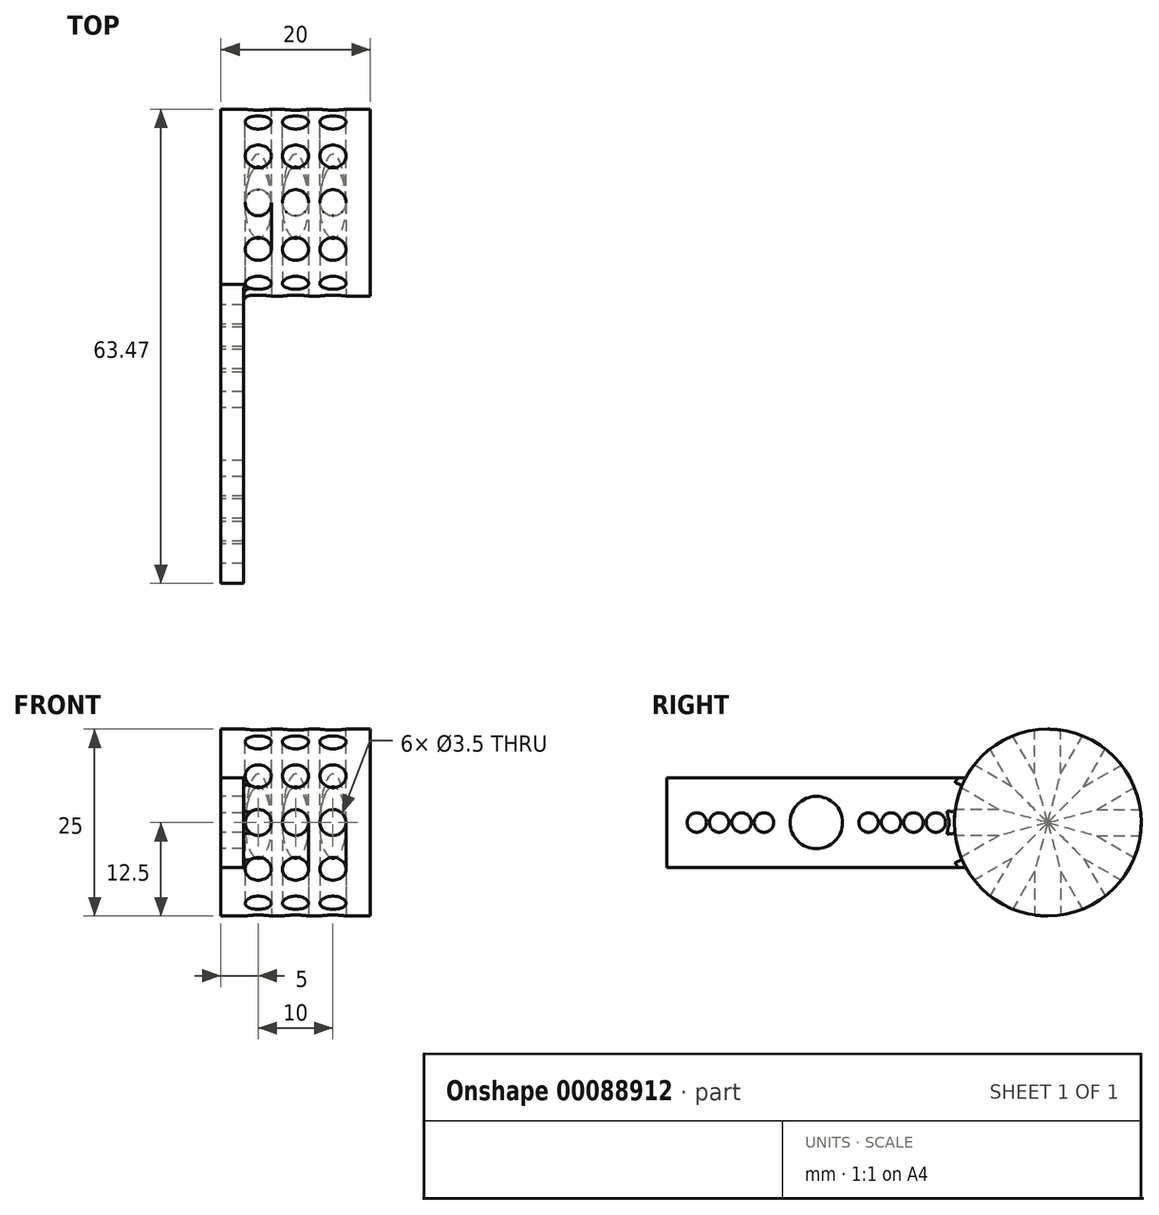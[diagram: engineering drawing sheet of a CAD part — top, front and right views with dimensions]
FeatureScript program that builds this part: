
annotation { "Feature Type Name" : "Feature", "Feature Type Description" : "" }
export const myFeature = defineFeature(function(context is Context, id is Id, definition is map)
    precondition{}
    {
        {
            var Q0;
            Q0=qCreatedBy(makeId("Right.planeOp"),FACE);
            var sketch = newSketch(context, id + "F0", { "sketchPlane" : qUnion([Q0])});
            skLineSegment(sketch, "E0.bottom", {"start": v(0, 12) * mm, "end": v(40, 12) * mm});
            skLineSegment(sketch, "E0.top", {"start": v(0, 0) * mm, "end": v(40, 0) * mm});
            skLineSegment(sketch, "E0.left", {"start": v(0, 12) * mm, "end": v(0, 0) * mm});
            skLineSegment(sketch, "E0.right", {"start": v(40, 12) * mm, "end": v(40, 0) * mm});
            skLineSegment(sketch, "E1", {"start": v(-4.67, 6) * mm, "end": v(58.67, 6) * mm, "construction": true});
            skLineSegment(sketch, "E2", {"start": v(20, 18.3) * mm, "end": v(20, -9.77) * mm, "construction": true});
            skCircle(sketch, "E3", {"center": v(20, 6) * mm, "radius": 3.5 * mm});
            skCircle(sketch, "E4", {"center": v(27, 6) * mm, "radius": 1.3 * mm});
            skCircle(sketch, "E5.1.0.0", {"center": v(30, 6) * mm, "radius": 1.3 * mm});
            skCircle(sketch, "E5.2.0.0", {"center": v(33, 6) * mm, "radius": 1.3 * mm});
            skCircle(sketch, "E5.3.0.0", {"center": v(36, 6) * mm, "radius": 1.3 * mm});
            skLineSegment(sketch, "E5.direction1", {"start": v(27, 6) * mm, "end": v(30, 6) * mm, "construction": true});
            skCircle(sketch, "E6.MirrorC", {"center": v(4, 6) * mm, "radius": 1.3 * mm});
            skCircle(sketch, "E7.MirrorC", {"center": v(7, 6) * mm, "radius": 1.3 * mm});
            skCircle(sketch, "E8.MirrorC", {"center": v(10, 6) * mm, "radius": 1.3 * mm});
            skCircle(sketch, "E9.MirrorC", {"center": v(13, 6) * mm, "radius": 1.3 * mm});
            skSolve(sketch);
        }
        {
            var Q0;
            Q0 = qSketchRegion(id + "F0", true);
            extrude(context, id + "F1", {"entities" : qUnion([Q0]), "depth" : 3 * mm});
        }
        {
            var Q0;
            Q0=makeQuery(id+"F1.opExtrude","CAP_FACE",FACE,{"disambiguationData":[OSD([sQuery(id+"F0.wireOp",EDGE,"E0.bottom"),sQuery(id+"F0.wireOp",EDGE,"E0.top"),sQuery(id+"F0.wireOp",EDGE,"E0.left"),sQuery(id+"F0.wireOp",EDGE,"E0.right"),sQuery(id+"F0.wireOp",EDGE,"E3"),sQuery(id+"F0.wireOp",EDGE,"E4"),sQuery(id+"F0.wireOp",EDGE,"E5.1.0.0"),sQuery(id+"F0.wireOp",EDGE,"E5.2.0.0"),sQuery(id+"F0.wireOp",EDGE,"E5.3.0.0"),sQuery(id+"F0.wireOp",EDGE,"E6.MirrorC"),sQuery(id+"F0.wireOp",EDGE,"E7.MirrorC"),sQuery(id+"F0.wireOp",EDGE,"E8.MirrorC"),sQuery(id+"F0.wireOp",EDGE,"E9.MirrorC")])],"isStart":true});
            var sketch = newSketch(context, id + "F2", { "sketchPlane" : qUnion([Q0])});
            skCircle(sketch, "E10", {"center": v(-50.97, 6) * mm, "radius": 12.5 * mm});
            skSolve(sketch);
        }
        {
            var Q0;
            Q0 = qSketchRegion(id + "F2", true);
            extrude(context, id + "F3", {"entities" : qUnion([Q0]), "operationType" : NewBodyOperationType.ADD, "oppositeDirection" : true, "depth" : 20 * mm});
        }
        {
            var Q0;
            Q0=makeQuery(id+"F1.opExtrude","SWEPT_FACE",FACE,{"disambiguationData":[OSD([sQuery(id+"F0.wireOp",EDGE,"E0.bottom")])]});
            var Q1;
            Q1=makeQuery(id+"F1.opExtrude","SWEPT_FACE",FACE,{"disambiguationData":[OSD([sQuery(id+"F0.wireOp",EDGE,"E0.top")])]});
            cPlane(context, id + "F4", {"entities" : qUnion([Q0, Q1]), "cplaneType" : CPlaneType.MID_PLANE, "offset" : 150 * mm, "width" : 150 * mm, "height" : 150 * mm});
        }
        {
            var Q0;
            Q0=qCreatedBy(id+"F4.planeOp",FACE);
            cPlane(context, id + "F5", {"entities" : qUnion([Q0]), "cplaneType" : CPlaneType.OFFSET, "offset" : 12.5 * mm, "width" : 150 * mm, "height" : 150 * mm});
        }
        {
            var Q0;
            Q0=qCreatedBy(id+"F5.planeOp",FACE);
            var sketch = newSketch(context, id + "F6", { "sketchPlane" : qUnion([Q0])});
            skLineSegment(sketch, "E11", {"start": v(-38.02, 50.97) * mm, "end": v(35.5, 50.97) * mm, "construction": true});
            skCircle(sketch, "E12", {"center": v(10, 50.97) * mm, "radius": 1.75 * mm});
            skCircle(sketch, "E13", {"center": v(5, 50.97) * mm, "radius": 1.75 * mm});
            skLineSegment(sketch, "E14", {"start": v(10, 31.53) * mm, "end": v(10, 69.48) * mm, "construction": true});
            skCircle(sketch, "E15.MirrorC", {"center": v(15, 50.97) * mm, "radius": 1.75 * mm});
            skSolve(sketch);
        }
        {
            var Q0;
            Q0 = qSketchRegion(id + "F6", true);
            extrude(context, id + "F7", {"entities" : qUnion([Q0]), "oppositeDirection" : true, "depth" : 12.5 * mm});
        }
        {
            var Q0;
            Q0=makeQuery(id+"F7.opExtrude","SWEPT_BODY",BODY,{"disambiguationData":[OSD([sQuery(id+"F6.wireOp",EDGE,"E12")])]});
            var Q1;
            Q1=makeQuery(id+"F7.opExtrude","SWEPT_BODY",BODY,{"disambiguationData":[OSD([sQuery(id+"F6.wireOp",EDGE,"E13")])]});
            var Q2;
            Q2=makeQuery(id+"F7.opExtrude","SWEPT_BODY",BODY,{"disambiguationData":[OSD([sQuery(id+"F6.wireOp",EDGE,"E15.MirrorC")])]});
            var Q3;
            Q3=sQuery(id+"F2.wireOp",EDGE,"E10");
            circularPattern(context, id + "F8", {"entities" : qUnion([Q0, Q1, Q2]), "axis" : qUnion([Q3]), "angle" : 360 * degree, "instanceCount" : 12, "equalSpace" : true});
        }
        {
            var Q0;
            Q0=makeQuery(id+"F7.opExtrude","SWEPT_BODY",BODY,{"disambiguationData":[OSD([sQuery(id+"F6.wireOp",EDGE,"E12")])]});
            var Q1;
            Q1=makeQuery(id+"F7.opExtrude","SWEPT_BODY",BODY,{"disambiguationData":[OSD([sQuery(id+"F6.wireOp",EDGE,"E13")])]});
            var Q2;
            Q2=makeQuery(id+"F7.opExtrude","SWEPT_BODY",BODY,{"disambiguationData":[OSD([sQuery(id+"F6.wireOp",EDGE,"E15.MirrorC")])]});
            var Q3;
            Q3=makeQuery(id+"F8.opPattern","COPY",BODY,{"derivedFrom":makeQuery(id+"F7.opExtrude","SWEPT_BODY",BODY,{"disambiguationData":[OSD([sQuery(id+"F6.wireOp",EDGE,"E12")])]}),"instanceName":"1"});
            var Q4;
            Q4=makeQuery(id+"F8.opPattern","COPY",BODY,{"derivedFrom":makeQuery(id+"F7.opExtrude","SWEPT_BODY",BODY,{"disambiguationData":[OSD([sQuery(id+"F6.wireOp",EDGE,"E13")])]}),"instanceName":"1"});
            var Q5;
            Q5=makeQuery(id+"F8.opPattern","COPY",BODY,{"derivedFrom":makeQuery(id+"F7.opExtrude","SWEPT_BODY",BODY,{"disambiguationData":[OSD([sQuery(id+"F6.wireOp",EDGE,"E15.MirrorC")])]}),"instanceName":"1"});
            var Q6;
            Q6=makeQuery(id+"F8.opPattern","COPY",BODY,{"derivedFrom":makeQuery(id+"F7.opExtrude","SWEPT_BODY",BODY,{"disambiguationData":[OSD([sQuery(id+"F6.wireOp",EDGE,"E12")])]}),"instanceName":"2"});
            var Q7;
            Q7=makeQuery(id+"F8.opPattern","COPY",BODY,{"derivedFrom":makeQuery(id+"F7.opExtrude","SWEPT_BODY",BODY,{"disambiguationData":[OSD([sQuery(id+"F6.wireOp",EDGE,"E13")])]}),"instanceName":"2"});
            var Q8;
            Q8=makeQuery(id+"F8.opPattern","COPY",BODY,{"derivedFrom":makeQuery(id+"F7.opExtrude","SWEPT_BODY",BODY,{"disambiguationData":[OSD([sQuery(id+"F6.wireOp",EDGE,"E15.MirrorC")])]}),"instanceName":"2"});
            var Q9;
            Q9=makeQuery(id+"F8.opPattern","COPY",BODY,{"derivedFrom":makeQuery(id+"F7.opExtrude","SWEPT_BODY",BODY,{"disambiguationData":[OSD([sQuery(id+"F6.wireOp",EDGE,"E12")])]}),"instanceName":"3"});
            var Q10;
            Q10=makeQuery(id+"F8.opPattern","COPY",BODY,{"derivedFrom":makeQuery(id+"F7.opExtrude","SWEPT_BODY",BODY,{"disambiguationData":[OSD([sQuery(id+"F6.wireOp",EDGE,"E13")])]}),"instanceName":"3"});
            var Q11;
            Q11=makeQuery(id+"F8.opPattern","COPY",BODY,{"derivedFrom":makeQuery(id+"F7.opExtrude","SWEPT_BODY",BODY,{"disambiguationData":[OSD([sQuery(id+"F6.wireOp",EDGE,"E15.MirrorC")])]}),"instanceName":"3"});
            var Q12;
            Q12=makeQuery(id+"F8.opPattern","COPY",BODY,{"derivedFrom":makeQuery(id+"F7.opExtrude","SWEPT_BODY",BODY,{"disambiguationData":[OSD([sQuery(id+"F6.wireOp",EDGE,"E12")])]}),"instanceName":"4"});
            var Q13;
            Q13=makeQuery(id+"F8.opPattern","COPY",BODY,{"derivedFrom":makeQuery(id+"F7.opExtrude","SWEPT_BODY",BODY,{"disambiguationData":[OSD([sQuery(id+"F6.wireOp",EDGE,"E13")])]}),"instanceName":"4"});
            var Q14;
            Q14=makeQuery(id+"F8.opPattern","COPY",BODY,{"derivedFrom":makeQuery(id+"F7.opExtrude","SWEPT_BODY",BODY,{"disambiguationData":[OSD([sQuery(id+"F6.wireOp",EDGE,"E15.MirrorC")])]}),"instanceName":"4"});
            var Q15;
            Q15=makeQuery(id+"F8.opPattern","COPY",BODY,{"derivedFrom":makeQuery(id+"F7.opExtrude","SWEPT_BODY",BODY,{"disambiguationData":[OSD([sQuery(id+"F6.wireOp",EDGE,"E12")])]}),"instanceName":"5"});
            var Q16;
            Q16=makeQuery(id+"F8.opPattern","COPY",BODY,{"derivedFrom":makeQuery(id+"F7.opExtrude","SWEPT_BODY",BODY,{"disambiguationData":[OSD([sQuery(id+"F6.wireOp",EDGE,"E13")])]}),"instanceName":"5"});
            var Q17;
            Q17=makeQuery(id+"F8.opPattern","COPY",BODY,{"derivedFrom":makeQuery(id+"F7.opExtrude","SWEPT_BODY",BODY,{"disambiguationData":[OSD([sQuery(id+"F6.wireOp",EDGE,"E15.MirrorC")])]}),"instanceName":"5"});
            var Q18;
            Q18=makeQuery(id+"F8.opPattern","COPY",BODY,{"derivedFrom":makeQuery(id+"F7.opExtrude","SWEPT_BODY",BODY,{"disambiguationData":[OSD([sQuery(id+"F6.wireOp",EDGE,"E12")])]}),"instanceName":"6"});
            var Q19;
            Q19=makeQuery(id+"F8.opPattern","COPY",BODY,{"derivedFrom":makeQuery(id+"F7.opExtrude","SWEPT_BODY",BODY,{"disambiguationData":[OSD([sQuery(id+"F6.wireOp",EDGE,"E13")])]}),"instanceName":"6"});
            var Q20;
            Q20=makeQuery(id+"F8.opPattern","COPY",BODY,{"derivedFrom":makeQuery(id+"F7.opExtrude","SWEPT_BODY",BODY,{"disambiguationData":[OSD([sQuery(id+"F6.wireOp",EDGE,"E15.MirrorC")])]}),"instanceName":"6"});
            var Q21;
            Q21=makeQuery(id+"F8.opPattern","COPY",BODY,{"derivedFrom":makeQuery(id+"F7.opExtrude","SWEPT_BODY",BODY,{"disambiguationData":[OSD([sQuery(id+"F6.wireOp",EDGE,"E12")])]}),"instanceName":"7"});
            var Q22;
            Q22=makeQuery(id+"F8.opPattern","COPY",BODY,{"derivedFrom":makeQuery(id+"F7.opExtrude","SWEPT_BODY",BODY,{"disambiguationData":[OSD([sQuery(id+"F6.wireOp",EDGE,"E13")])]}),"instanceName":"7"});
            var Q23;
            Q23=makeQuery(id+"F8.opPattern","COPY",BODY,{"derivedFrom":makeQuery(id+"F7.opExtrude","SWEPT_BODY",BODY,{"disambiguationData":[OSD([sQuery(id+"F6.wireOp",EDGE,"E15.MirrorC")])]}),"instanceName":"7"});
            var Q24;
            Q24=makeQuery(id+"F8.opPattern","COPY",BODY,{"derivedFrom":makeQuery(id+"F7.opExtrude","SWEPT_BODY",BODY,{"disambiguationData":[OSD([sQuery(id+"F6.wireOp",EDGE,"E12")])]}),"instanceName":"8"});
            var Q25;
            Q25=makeQuery(id+"F8.opPattern","COPY",BODY,{"derivedFrom":makeQuery(id+"F7.opExtrude","SWEPT_BODY",BODY,{"disambiguationData":[OSD([sQuery(id+"F6.wireOp",EDGE,"E13")])]}),"instanceName":"8"});
            var Q26;
            Q26=makeQuery(id+"F8.opPattern","COPY",BODY,{"derivedFrom":makeQuery(id+"F7.opExtrude","SWEPT_BODY",BODY,{"disambiguationData":[OSD([sQuery(id+"F6.wireOp",EDGE,"E15.MirrorC")])]}),"instanceName":"8"});
            var Q27;
            Q27=makeQuery(id+"F8.opPattern","COPY",BODY,{"derivedFrom":makeQuery(id+"F7.opExtrude","SWEPT_BODY",BODY,{"disambiguationData":[OSD([sQuery(id+"F6.wireOp",EDGE,"E12")])]}),"instanceName":"9"});
            var Q28;
            Q28=makeQuery(id+"F8.opPattern","COPY",BODY,{"derivedFrom":makeQuery(id+"F7.opExtrude","SWEPT_BODY",BODY,{"disambiguationData":[OSD([sQuery(id+"F6.wireOp",EDGE,"E13")])]}),"instanceName":"9"});
            var Q29;
            Q29=makeQuery(id+"F8.opPattern","COPY",BODY,{"derivedFrom":makeQuery(id+"F7.opExtrude","SWEPT_BODY",BODY,{"disambiguationData":[OSD([sQuery(id+"F6.wireOp",EDGE,"E15.MirrorC")])]}),"instanceName":"9"});
            var Q30;
            Q30=makeQuery(id+"F8.opPattern","COPY",BODY,{"derivedFrom":makeQuery(id+"F7.opExtrude","SWEPT_BODY",BODY,{"disambiguationData":[OSD([sQuery(id+"F6.wireOp",EDGE,"E12")])]}),"instanceName":"10"});
            var Q31;
            Q31=makeQuery(id+"F8.opPattern","COPY",BODY,{"derivedFrom":makeQuery(id+"F7.opExtrude","SWEPT_BODY",BODY,{"disambiguationData":[OSD([sQuery(id+"F6.wireOp",EDGE,"E13")])]}),"instanceName":"10"});
            var Q32;
            Q32=makeQuery(id+"F8.opPattern","COPY",BODY,{"derivedFrom":makeQuery(id+"F7.opExtrude","SWEPT_BODY",BODY,{"disambiguationData":[OSD([sQuery(id+"F6.wireOp",EDGE,"E15.MirrorC")])]}),"instanceName":"10"});
            var Q33;
            Q33=makeQuery(id+"F8.opPattern","COPY",BODY,{"derivedFrom":makeQuery(id+"F7.opExtrude","SWEPT_BODY",BODY,{"disambiguationData":[OSD([sQuery(id+"F6.wireOp",EDGE,"E12")])]}),"instanceName":"11"});
            var Q34;
            Q34=makeQuery(id+"F8.opPattern","COPY",BODY,{"derivedFrom":makeQuery(id+"F7.opExtrude","SWEPT_BODY",BODY,{"disambiguationData":[OSD([sQuery(id+"F6.wireOp",EDGE,"E13")])]}),"instanceName":"11"});
            var Q35;
            Q35=makeQuery(id+"F8.opPattern","COPY",BODY,{"derivedFrom":makeQuery(id+"F7.opExtrude","SWEPT_BODY",BODY,{"disambiguationData":[OSD([sQuery(id+"F6.wireOp",EDGE,"E15.MirrorC")])]}),"instanceName":"11"});
            var Q36;
            Q36=makeQuery(id+"F8.opPattern","COPY",BODY,{"derivedFrom":makeQuery(id+"F7.opExtrude","SWEPT_BODY",BODY,{"disambiguationData":[OSD([sQuery(id+"F6.wireOp",EDGE,"E12")])]}),"instanceName":"12"});
            var Q37;
            Q37=makeQuery(id+"F8.opPattern","COPY",BODY,{"derivedFrom":makeQuery(id+"F7.opExtrude","SWEPT_BODY",BODY,{"disambiguationData":[OSD([sQuery(id+"F6.wireOp",EDGE,"E13")])]}),"instanceName":"12"});
            var Q38;
            Q38=makeQuery(id+"F8.opPattern","COPY",BODY,{"derivedFrom":makeQuery(id+"F7.opExtrude","SWEPT_BODY",BODY,{"disambiguationData":[OSD([sQuery(id+"F6.wireOp",EDGE,"E15.MirrorC")])]}),"instanceName":"12"});
            var Q39;
            Q39=makeQuery(id+"F1.opExtrude","SWEPT_BODY",BODY,{"disambiguationData":[OSD([sQuery(id+"F0.wireOp",EDGE,"E0.bottom"),sQuery(id+"F0.wireOp",EDGE,"E0.top"),sQuery(id+"F0.wireOp",EDGE,"E0.left"),sQuery(id+"F0.wireOp",EDGE,"E0.right"),sQuery(id+"F0.wireOp",EDGE,"E3"),sQuery(id+"F0.wireOp",EDGE,"E4"),sQuery(id+"F0.wireOp",EDGE,"E5.1.0.0"),sQuery(id+"F0.wireOp",EDGE,"E5.2.0.0"),sQuery(id+"F0.wireOp",EDGE,"E5.3.0.0"),sQuery(id+"F0.wireOp",EDGE,"E6.MirrorC"),sQuery(id+"F0.wireOp",EDGE,"E7.MirrorC"),sQuery(id+"F0.wireOp",EDGE,"E8.MirrorC"),sQuery(id+"F0.wireOp",EDGE,"E9.MirrorC")])]});
            booleanBodies(context, id + "F9", {"operationType" : BooleanOperationType.SUBTRACTION, "tools" : qUnion([Q0, Q1, Q2, Q3, Q4, Q5, Q6, Q7, Q8, Q9, Q10, Q11, Q12, Q13, Q14, Q15, Q16, Q17, Q18, Q19, Q20, Q21, Q22, Q23, Q24, Q25, Q26, Q27, Q28, Q29, Q30, Q31, Q32, Q33, Q34, Q35, Q36, Q37, Q38]), "targets" : qUnion([Q39])});
        }
        {
            var Q0;
            Q0=makeQuery(id+"F3.boolean.opBoolean","INTERSECT",EDGE,{"derivedFrom":[makeQuery(id+"F1.opExtrude","CAP_FACE",FACE,{"disambiguationData":[OSD([sQuery(id+"F0.wireOp",EDGE,"E0.bottom"),sQuery(id+"F0.wireOp",EDGE,"E0.top"),sQuery(id+"F0.wireOp",EDGE,"E0.left"),sQuery(id+"F0.wireOp",EDGE,"E0.right"),sQuery(id+"F0.wireOp",EDGE,"E3"),sQuery(id+"F0.wireOp",EDGE,"E4"),sQuery(id+"F0.wireOp",EDGE,"E5.1.0.0"),sQuery(id+"F0.wireOp",EDGE,"E5.2.0.0"),sQuery(id+"F0.wireOp",EDGE,"E5.3.0.0"),sQuery(id+"F0.wireOp",EDGE,"E6.MirrorC"),sQuery(id+"F0.wireOp",EDGE,"E7.MirrorC"),sQuery(id+"F0.wireOp",EDGE,"E8.MirrorC"),sQuery(id+"F0.wireOp",EDGE,"E9.MirrorC")])],"isStart":false}),makeQuery(id+"F3.opExtrude","SWEPT_FACE",FACE,{"disambiguationData":[OSD([sQuery(id+"F2.wireOp",EDGE,"E10")])]})]});
            var Q1;
            Q1=makeQuery(id+"F1.opExtrude","SWEPT_EDGE",EDGE,{"disambiguationData":[OSD([sQuery(id+"F0.wireOp",EDGE,"E0.bottom"),sQuery(id+"F0.wireOp",EDGE,"E0.right")])]});
            var Q2;
            Q2=makeQuery(id+"F1.opExtrude","SWEPT_EDGE",EDGE,{"disambiguationData":[OSD([sQuery(id+"F0.wireOp",EDGE,"E0.top"),sQuery(id+"F0.wireOp",EDGE,"E0.right")])]});
            fillet(context, id + "F10", {"entities" : qUnion([Q0, Q1, Q2]), "radius" : 1 * mm, "tangentPropagation" : true, "allowEdgeOverflow" : false});
        }
    });
